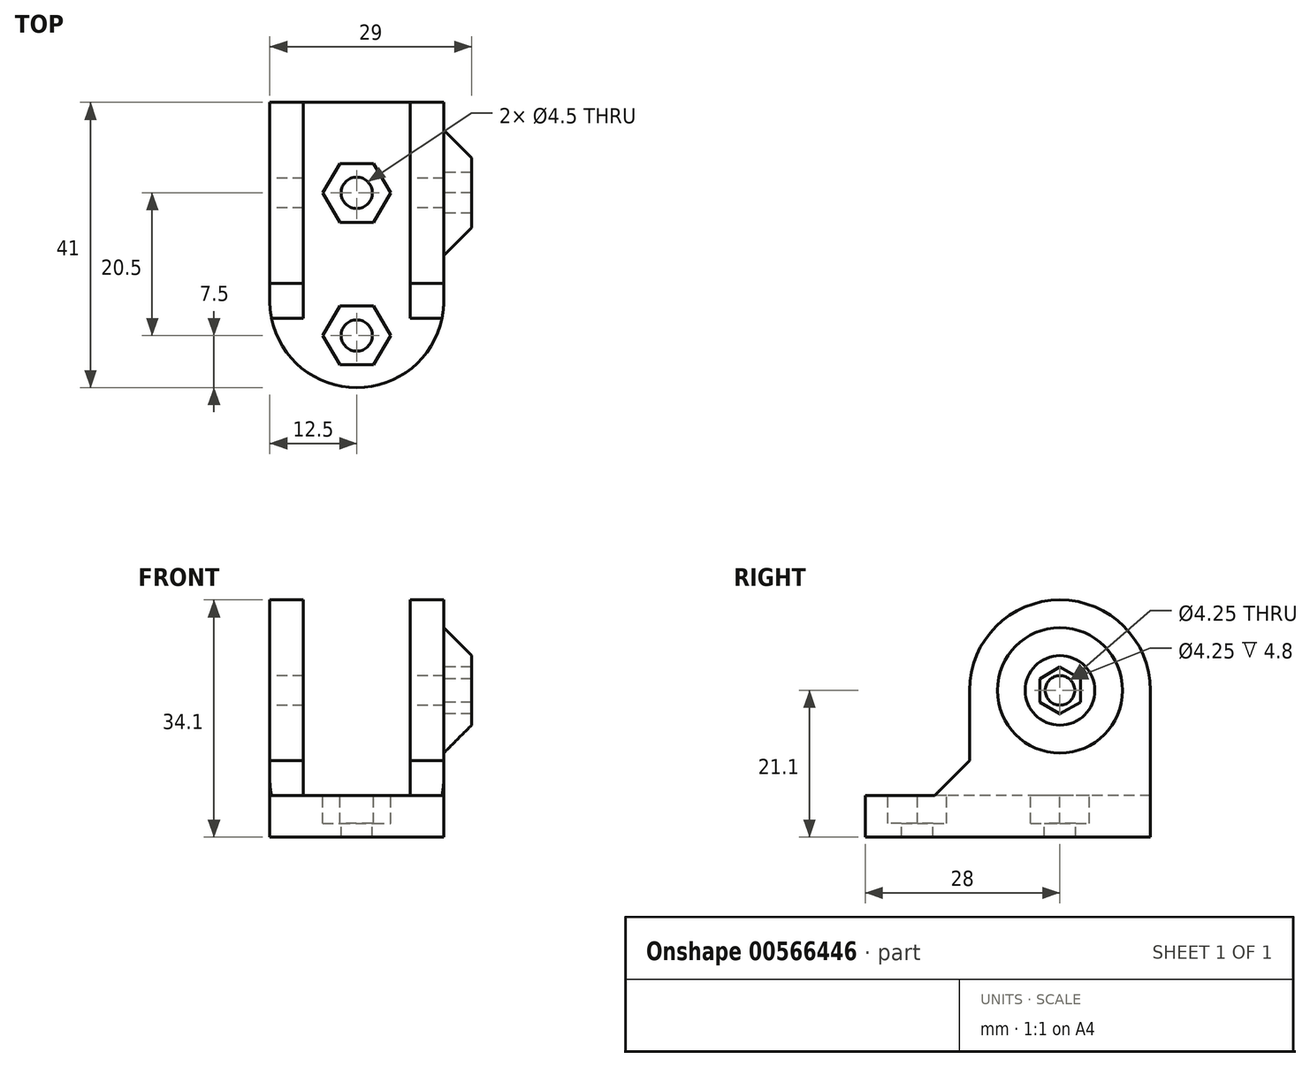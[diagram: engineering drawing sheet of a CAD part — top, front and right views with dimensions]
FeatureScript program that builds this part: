
annotation { "Feature Type Name" : "Feature", "Feature Type Description" : "" }
export const myFeature = defineFeature(function(context is Context, id is Id, definition is map)
    precondition{}
    {
        {
            var Q0;
            Q0=qCreatedBy(makeId("Right.planeOp"),FACE);
            var sketch = newSketch(context, id + "F0", { "sketchPlane" : qUnion([Q0])});
            skCircle(sketch, "E0", {"center": v(0, 0) * mm, "radius": 2.12 * mm});
            skArc(sketch, "E1", {"start": v(13, 0) * mm, "mid": v(0, 13) * mm, "end": v(-13, 0) * mm});
            skLineSegment(sketch, "E2", {"start": v(-13, 0) * mm, "end": v(-13, -15.1) * mm});
            skLineSegment(sketch, "E3", {"start": v(-13, -15.1) * mm, "end": v(-28, -15.1) * mm});
            skLineSegment(sketch, "E4", {"start": v(-28, -15.1) * mm, "end": v(-28, -21.1) * mm});
            skLineSegment(sketch, "E5", {"start": v(-28, -21.1) * mm, "end": v(0, -21.1) * mm});
            skLineSegment(sketch, "E6.MirrorCS", {"start": v(13, 0) * mm, "end": v(13, -15.1) * mm});
            skLineSegment(sketch, "E7", {"start": v(0, -21.1) * mm, "end": v(13, -21.1) * mm});
            skLineSegment(sketch, "E8", {"start": v(13, -21.1) * mm, "end": v(13, -15.1) * mm});
            skSolve(sketch);
        }
        {
            var Q0;
            Q0=qSketchRegion(id+"F0",true);
            extrude(context, id + "F1", {"entities" : qUnion([Q0]), "endBound" : BoundingType.SYMMETRIC, "depth" : 25 * mm, "offsetDistance" : 25 * mm});
        }
        {
            var Q0;
            Q0=makeQuery(id+"F1.opExtrude","SWEPT_FACE",FACE,{"disambiguationData":[OSD([sQuery(id+"F0.wireOp",EDGE,"E3")])]});
            var sketch = newSketch(context, id + "F2", { "sketchPlane" : qUnion([Q0])});
            skLineSegment(sketch, "E9.bottom", {"start": v(-7.7, 13) * mm, "end": v(7.7, 13) * mm});
            skLineSegment(sketch, "E9.top", {"start": v(-7.7, -13) * mm, "end": v(7.7, -13) * mm});
            skLineSegment(sketch, "E9.left", {"start": v(-7.7, 13) * mm, "end": v(-7.7, -13) * mm});
            skLineSegment(sketch, "E9.right", {"start": v(7.7, 13) * mm, "end": v(7.7, -13) * mm});
            skSolve(sketch);
        }
        {
            var Q0;
            Q0=qSketchRegion(id+"F2",true);
            extrude(context, id + "F3", {"entities" : qUnion([Q0]), "operationType" : NewBodyOperationType.REMOVE, "endBound" : BoundingType.THROUGH_ALL, "depth" : 25 * mm, "offsetDistance" : 25 * mm});
        }
        {
            var Q0;
            Q0=makeQuery(id+"F3.boolean.opBoolean","MERGE",FACE,{"derivedFrom":[makeQuery(id+"F1.opExtrude","SWEPT_FACE",FACE,{"disambiguationData":[OSD([sQuery(id+"F0.wireOp",EDGE,"E3")])]}),makeQuery(id+"F1.opExtrude","SWEPT_FACE",FACE,{"disambiguationData":[OSD([sQuery(id+"F0.wireOp",EDGE,"134ed93e-5797-451a-8282-cf3413b09aac0.MirrorCS")])]}),makeQuery(id+"F3.opExtrude","CAP_FACE",FACE,{"disambiguationData":[OSD([sQuery(id+"F2.wireOp",EDGE,"E9.bottom"),sQuery(id+"F2.wireOp",EDGE,"E9.top"),sQuery(id+"F2.wireOp",EDGE,"E9.left"),sQuery(id+"F2.wireOp",EDGE,"E9.right")])],"isStart":true})]});
            var sketch = newSketch(context, id + "F4", { "sketchPlane" : qUnion([Q0])});
            skCircle(sketch, "E10", {"center": v(0, 20.5) * mm, "radius": 2.25 * mm, "construction": true});
            skCircle(sketch, "E11.MirrorC", {"center": v(0, -20.5) * mm, "radius": 2.25 * mm});
            skCircle(sketch, "E12", {"center": v(0, 0) * mm, "radius": 2.25 * mm});
            skSolve(sketch);
        }
        {
            var Q0;
            Q0=qSketchRegion(id+"F4",true);
            extrude(context, id + "F5", {"entities" : qUnion([Q0]), "operationType" : NewBodyOperationType.REMOVE, "oppositeDirection" : true, "depth" : 25 * mm, "offsetDistance" : 25 * mm});
        }
        {
            var Q0;
            Q0=makeQuery(id+"F3.boolean.opBoolean","MERGE",FACE,{"derivedFrom":[makeQuery(id+"F1.opExtrude","SWEPT_FACE",FACE,{"disambiguationData":[OSD([sQuery(id+"F0.wireOp",EDGE,"E3")])]}),makeQuery(id+"F1.opExtrude","SWEPT_FACE",FACE,{"disambiguationData":[OSD([sQuery(id+"F0.wireOp",EDGE,"134ed93e-5797-451a-8282-cf3413b09aac0.MirrorCS")])]}),makeQuery(id+"F3.opExtrude","CAP_FACE",FACE,{"disambiguationData":[OSD([sQuery(id+"F2.wireOp",EDGE,"E9.bottom"),sQuery(id+"F2.wireOp",EDGE,"E9.top"),sQuery(id+"F2.wireOp",EDGE,"E9.left"),sQuery(id+"F2.wireOp",EDGE,"E9.right")])],"isStart":true})]});
            var sketch = newSketch(context, id + "F6", { "sketchPlane" : qUnion([Q0])});
            skCircle(sketch, "E13.cCircle", {"center": v(0, 20.5) * mm, "radius": 4.22 * mm, "construction": true});
            skLineSegment(sketch, "E13.0", {"start": v(4.88, 20.5) * mm, "end": v(2.44, 16.27) * mm, "construction": true});
            skLineSegment(sketch, "E13.1", {"start": v(2.44, 16.28) * mm, "end": v(-2.44, 16.28) * mm, "construction": true});
            skLineSegment(sketch, "E13.2", {"start": v(-2.44, 16.27) * mm, "end": v(-4.88, 20.5) * mm, "construction": true});
            skLineSegment(sketch, "E13.3", {"start": v(-4.88, 20.5) * mm, "end": v(-2.44, 24.73) * mm, "construction": true});
            skLineSegment(sketch, "E13.4", {"start": v(-2.44, 24.73) * mm, "end": v(2.44, 24.73) * mm, "construction": true});
            skLineSegment(sketch, "E13.5", {"start": v(2.44, 24.72) * mm, "end": v(4.88, 20.5) * mm, "construction": true});
            skPoint(sketch, "E13.0.midPoint", {"position": v(3.66, 18.39) * mm});
            skLineSegment(sketch, "E14.MirrorCS", {"start": v(-2.44, -24.73) * mm, "end": v(2.44, -24.73) * mm});
            skLineSegment(sketch, "E15.MirrorCS", {"start": v(2.44, -24.73) * mm, "end": v(4.88, -20.5) * mm});
            skLineSegment(sketch, "E16.MirrorCS", {"start": v(-4.88, -20.5) * mm, "end": v(-2.44, -24.73) * mm});
            skLineSegment(sketch, "E17.MirrorCS", {"start": v(-2.44, -16.27) * mm, "end": v(-4.88, -20.5) * mm});
            skLineSegment(sketch, "E18.MirrorCS", {"start": v(2.44, -16.28) * mm, "end": v(-2.44, -16.28) * mm});
            skLineSegment(sketch, "E19.MirrorCS", {"start": v(4.88, -20.5) * mm, "end": v(2.44, -16.28) * mm});
            skCircle(sketch, "E20.MirrorC", {"center": v(0, -20.5) * mm, "radius": 4.22 * mm, "construction": true});
            skPoint(sketch, "E21.MirrorP", {"position": v(3.66, -18.39) * mm});
            skCircle(sketch, "E22.cCircle", {"center": v(0, 0) * mm, "radius": 4.22 * mm, "construction": true});
            skLineSegment(sketch, "E22.0", {"start": v(-2.44, 4.22) * mm, "end": v(2.44, 4.22) * mm});
            skLineSegment(sketch, "E22.1", {"start": v(2.44, 4.22) * mm, "end": v(4.88, 0) * mm});
            skLineSegment(sketch, "E22.2", {"start": v(4.88, 0) * mm, "end": v(2.44, -4.22) * mm});
            skLineSegment(sketch, "E22.3", {"start": v(2.44, -4.22) * mm, "end": v(-2.44, -4.22) * mm});
            skLineSegment(sketch, "E22.4", {"start": v(-2.44, -4.23) * mm, "end": v(-4.88, 0) * mm});
            skLineSegment(sketch, "E22.5", {"start": v(-4.88, 0) * mm, "end": v(-2.44, 4.22) * mm});
            skPoint(sketch, "E22.0.midPoint", {"position": v(0, 4.22) * mm});
            skSolve(sketch);
        }
        {
            var Q0;
            Q0=qSketchRegion(id+"F6",true);
            extrude(context, id + "F7", {"entities" : qUnion([Q0]), "operationType" : NewBodyOperationType.REMOVE, "oppositeDirection" : true, "depth" : 4 * mm, "offsetDistance" : 25 * mm});
        }
        {
            var Q0;
            Q0=makeQuery(id+"F1.opExtrude","CAP_EDGE",EDGE,{"disambiguationData":[OSD([sQuery(id+"F0.wireOp",EDGE,"9956f1e4-fb87-4a73-b4c6-8dad2b9d14270.MirrorCS")])],"isStart":false});
            var Q1;
            Q1=makeQuery(id+"F1.opExtrude","CAP_EDGE",EDGE,{"disambiguationData":[OSD([sQuery(id+"F0.wireOp",EDGE,"9956f1e4-fb87-4a73-b4c6-8dad2b9d14270.MirrorCS")])],"isStart":true});
            var Q2;
            Q2=makeQuery(id+"F1.opExtrude","CAP_EDGE",EDGE,{"disambiguationData":[OSD([sQuery(id+"F0.wireOp",EDGE,"E4")])],"isStart":true});
            var Q3;
            Q3=makeQuery(id+"F1.opExtrude","CAP_EDGE",EDGE,{"disambiguationData":[OSD([sQuery(id+"F0.wireOp",EDGE,"E4")])],"isStart":false});
            fillet(context, id + "F8", {"entities" : qUnion([Q0, Q1, Q2, Q3]), "radius" : 12.5 * mm, "tangentPropagation" : true, "allowEdgeOverflow" : false});
        }
        {
            var Q0;
            {var subQ0=sQuery(id+"F0.wireOp",EDGE,"E3");var subQ1=sQuery(id+"F2.wireOp",EDGE,"E9.left");var subQ3=sQuery(id+"F0.wireOp",EDGE,"E2");Q0=makeQuery(id+"F3.boolean.opBoolean","SPLIT",EDGE,{"disambiguationData":[TD([makeQuery(id+"F3.opExtrude","SWEPT_FACE",FACE,{"disambiguationData":[OSD([subQ1])]})])],"derivedFrom":makeQuery(id+"F1.opExtrude","SWEPT_EDGE",EDGE,{"disambiguationData":[OSD([subQ3,subQ0])]})});}
            var Q1;
            {var subQ0=sQuery(id+"F0.wireOp",EDGE,"E3");var subQ2=sQuery(id+"F0.wireOp",EDGE,"E2");var subQ3=sQuery(id+"F2.wireOp",EDGE,"E9.right");Q1=makeQuery(id+"F3.boolean.opBoolean","SPLIT",EDGE,{"disambiguationData":[TD([makeQuery(id+"F3.opExtrude","SWEPT_FACE",FACE,{"disambiguationData":[OSD([subQ3])]})])],"derivedFrom":makeQuery(id+"F1.opExtrude","SWEPT_EDGE",EDGE,{"disambiguationData":[OSD([subQ2,subQ0])]})});}
            var Q2;
            {var subQ0=sQuery(id+"F0.wireOp",EDGE,"134ed93e-5797-451a-8282-cf3413b09aac0.MirrorCS");var subQ1=sQuery(id+"F0.wireOp",EDGE,"E6.MirrorCS");var subQ3=sQuery(id+"F2.wireOp",EDGE,"E9.right");Q2=makeQuery(id+"F3.boolean.opBoolean","SPLIT",EDGE,{"disambiguationData":[TD([makeQuery(id+"F3.opExtrude","SWEPT_FACE",FACE,{"disambiguationData":[OSD([subQ3])]})])],"derivedFrom":makeQuery(id+"F1.opExtrude","SWEPT_EDGE",EDGE,{"disambiguationData":[OSD([subQ1,subQ0])]})});}
            var Q3;
            {var subQ0=sQuery(id+"F0.wireOp",EDGE,"134ed93e-5797-451a-8282-cf3413b09aac0.MirrorCS");var subQ1=sQuery(id+"F0.wireOp",EDGE,"E6.MirrorCS");var subQ3=sQuery(id+"F2.wireOp",EDGE,"E9.left");Q3=makeQuery(id+"F3.boolean.opBoolean","SPLIT",EDGE,{"disambiguationData":[TD([makeQuery(id+"F3.opExtrude","SWEPT_FACE",FACE,{"disambiguationData":[OSD([subQ3])]})])],"derivedFrom":makeQuery(id+"F1.opExtrude","SWEPT_EDGE",EDGE,{"disambiguationData":[OSD([subQ1,subQ0])]})});}
            chamfer(context, id + "F9", {"entities" : qUnion([Q0, Q1, Q2, Q3]), "width" : 5 * mm, "tangentPropagation" : true});
        }
        {
            var Q0;
            Q0=makeQuery(id+"F1.opExtrude","CAP_FACE",FACE,{"disambiguationData":[OSD([sQuery(id+"F0.wireOp",EDGE,"E0"),sQuery(id+"F0.wireOp",EDGE,"E1"),sQuery(id+"F0.wireOp",EDGE,"E2"),sQuery(id+"F0.wireOp",EDGE,"E3"),sQuery(id+"F0.wireOp",EDGE,"E4"),sQuery(id+"F0.wireOp",EDGE,"E5"),sQuery(id+"F0.wireOp",EDGE,"E6.MirrorCS"),sQuery(id+"F0.wireOp",EDGE,"E7"),sQuery(id+"F0.wireOp",EDGE,"E8")])],"isStart":false});
            var sketch = newSketch(context, id + "F10", { "sketchPlane" : qUnion([Q0])});
            skCircle(sketch, "E23.cCircle", {"center": v(0, 0) * mm, "radius": 2.92 * mm, "construction": true});
            skLineSegment(sketch, "E23.0", {"start": v(2.92, 1.69) * mm, "end": v(2.92, -1.69) * mm});
            skLineSegment(sketch, "E23.1", {"start": v(2.92, -1.69) * mm, "end": v(0, -3.37) * mm});
            skLineSegment(sketch, "E23.2", {"start": v(0, -3.37) * mm, "end": v(-2.92, -1.69) * mm});
            skLineSegment(sketch, "E23.3", {"start": v(-2.92, -1.69) * mm, "end": v(-2.92, 1.69) * mm});
            skLineSegment(sketch, "E23.4", {"start": v(-2.92, 1.69) * mm, "end": v(0, 3.37) * mm});
            skLineSegment(sketch, "E23.5", {"start": v(0, 3.37) * mm, "end": v(2.92, 1.69) * mm});
            skPoint(sketch, "E23.0.midPoint", {"position": v(2.92, 0) * mm});
            skCircle(sketch, "E24", {"center": v(0, 0) * mm, "radius": 5 * mm});
            skSolve(sketch);
        }
        {
            var Q0;
            Q0=qSketchRegion(id+"F10",true);
            extrude(context, id + "F11", {"entities" : qUnion([Q0]), "operationType" : NewBodyOperationType.ADD, "depth" : 4 * mm, "offsetDistance" : 25 * mm});
        }
        {
            var Q0;
            Q0=makeQuery(id+"F11.opExtrude","CAP_EDGE",EDGE,{"disambiguationData":[OSD([sQuery(id+"F10.wireOp",EDGE,"E24")])],"isStart":true});
            chamfer(context, id + "F12", {"entities" : qUnion([Q0]), "width" : 4 * mm, "tangentPropagation" : true});
        }
    });
